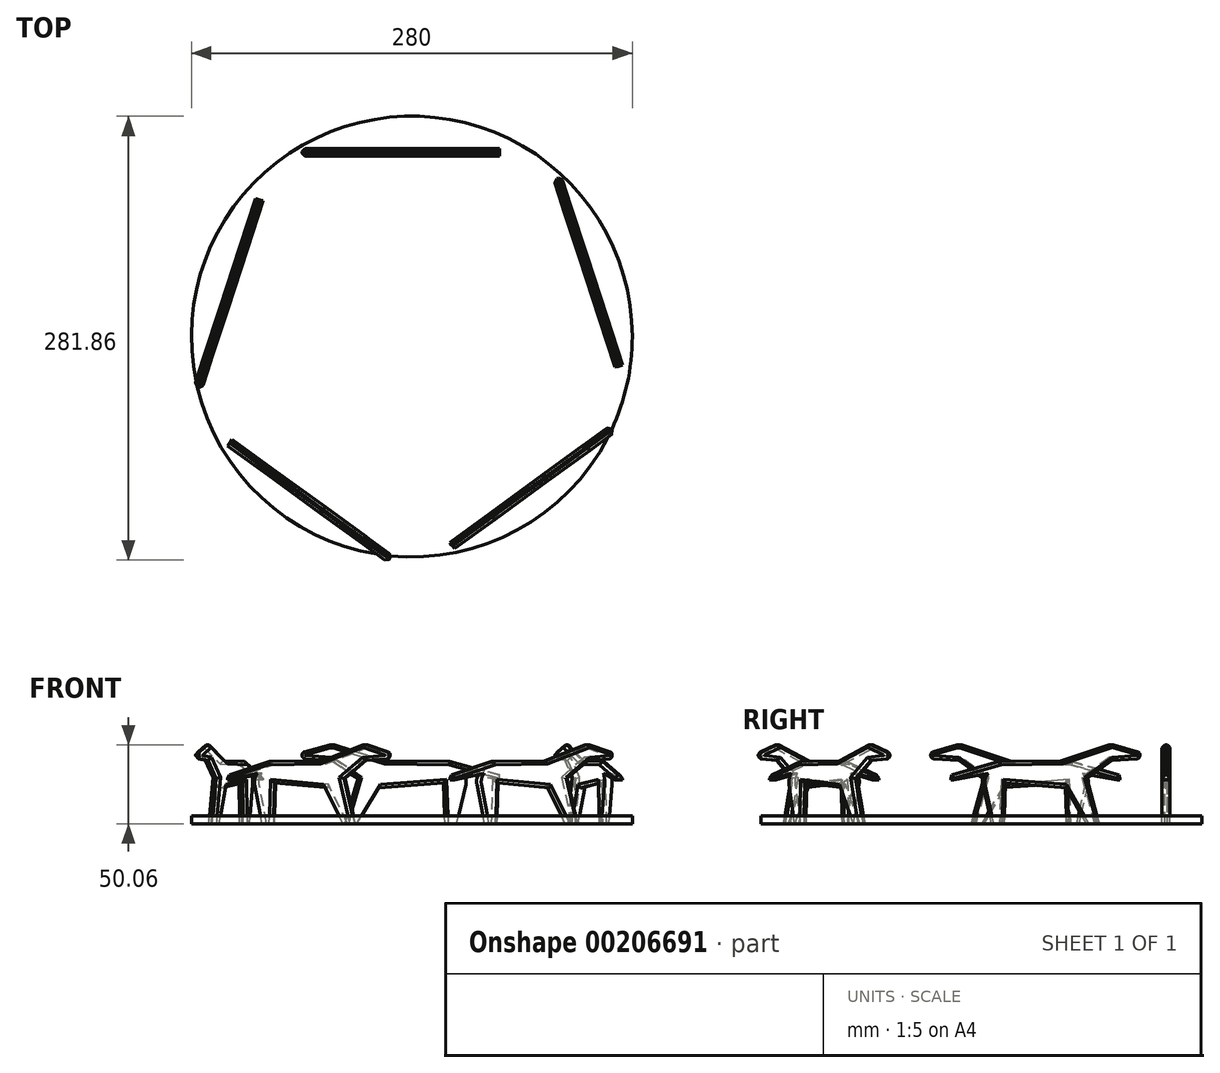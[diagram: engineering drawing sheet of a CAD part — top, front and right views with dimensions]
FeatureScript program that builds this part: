
annotation { "Feature Type Name" : "Feature", "Feature Type Description" : "" }
export const myFeature = defineFeature(function(context is Context, id is Id, definition is map)
    precondition{}
    {
        {
            var Q0;
            Q0=qCreatedBy(makeId("Front.planeOp"),FACE);
            var sketch = newSketch(context, id + "F0", { "sketchPlane" : qUnion([Q0])});
            skLineSegment(sketch, "E0", {"start": v(0, 30.49) * mm, "end": v(0, -33.76) * mm, "construction": true});
            skLineSegment(sketch, "E1", {"start": v(-37.33, 0) * mm, "end": v(42.96, 0) * mm, "construction": true});
            skArc(sketch, "E2", {"start": v(-21.11, 22.86) * mm, "mid": v(-24.39, 33.27) * mm, "end": v(-34.27, 28.64) * mm});
            skArc(sketch, "E3.MirrorC", {"start": v(20.07, 26.07) * mm, "mid": v(27.86, 33.86) * mm, "end": v(34.36, 24.97) * mm});
            skLineSegment(sketch, "E4", {"start": v(-42.5, 0) * mm, "end": v(-35.04, 0) * mm});
            skLineSegment(sketch, "E5", {"start": v(-35.04, 0) * mm, "end": v(-21.11, 22.86) * mm});
            skLineSegment(sketch, "E6", {"start": v(-42.5, 0) * mm, "end": v(-34.27, 28.64) * mm});
            skLineSegment(sketch, "E7", {"start": v(21.03, 0) * mm, "end": v(28.49, 0) * mm});
            skLineSegment(sketch, "E8", {"start": v(28.49, 0) * mm, "end": v(34.36, 24.97) * mm});
            skLineSegment(sketch, "E9", {"start": v(21.03, 0) * mm, "end": v(20.06, 26.37) * mm});
            skLineSegment(sketch, "E10", {"start": v(-21.11, 22.86) * mm, "end": v(20.07, 26.07) * mm});
            skArc(sketch, "E11", {"start": v(-52.04, 50.06) * mm, "mid": v(-50.83, 40.22) * mm, "end": v(-49.22, 50) * mm});
            skCircle(sketch, "E12", {"center": v(-67.49, 43.52) * mm, "radius": 2.27 * mm});
            skLineSegment(sketch, "E13", {"start": v(-68.08, 45.71) * mm, "end": v(-52.04, 50.06) * mm});
            skLineSegment(sketch, "E14", {"start": v(-67.63, 41.25) * mm, "end": v(-51.04, 40.22) * mm});
            skLineSegment(sketch, "E15", {"start": v(-51.04, 40.22) * mm, "end": v(-34.27, 28.64) * mm});
            skLineSegment(sketch, "E16", {"start": v(-49.22, 50) * mm, "end": v(-17.15, 39.88) * mm});
            skLineSegment(sketch, "E17", {"start": v(-17.15, 39.88) * mm, "end": v(24.08, 39.47) * mm});
            skLineSegment(sketch, "E18", {"start": v(24.08, 39.47) * mm, "end": v(55.59, 30.9) * mm});
            skLineSegment(sketch, "E19", {"start": v(55.59, 30.9) * mm, "end": v(55.59, 27.7) * mm});
            skLineSegment(sketch, "E20", {"start": v(55.59, 27.7) * mm, "end": v(32.22, 31.96) * mm});
            skLineSegment(sketch, "E21", {"start": v(-52.04, 50.06) * mm, "end": v(-49.22, 50) * mm});
            skSolve(sketch);
        }
        {
            var Q0;
            Q0 = qSketchRegion(id + "F0", true);
            extrude(context, id + "F1", {"entities" : qUnion([Q0]), "endBound" : BoundingType.SYMMETRIC, "depth" : 5 * mm});
        }
        {
            var Q0;
            Q0=makeQuery(id+"F1.opExtrude","CAP_EDGE",EDGE,{"disambiguationData":[OSD([sQuery(id+"F0.wireOp",EDGE,"E13")])],"isStart":false});
            var Q1;
            Q1=makeQuery(id+"F1.opExtrude","CAP_EDGE",EDGE,{"disambiguationData":[OSD([sQuery(id+"F0.wireOp",EDGE,"E21")])],"isStart":false});
            var Q2;
            Q2=makeQuery(id+"F1.opExtrude","CAP_EDGE",EDGE,{"disambiguationData":[OSD([sQuery(id+"F0.wireOp",EDGE,"E15")])],"isStart":false});
            var Q3;
            Q3=makeQuery(id+"F1.opExtrude","CAP_EDGE",EDGE,{"disambiguationData":[OSD([sQuery(id+"F0.wireOp",EDGE,"E6")])],"isStart":false});
            var Q4;
            Q4=makeQuery(id+"F1.opExtrude","CAP_EDGE",EDGE,{"disambiguationData":[OSD([sQuery(id+"F0.wireOp",EDGE,"E10")])],"isStart":false});
            var Q5;
            Q5=makeQuery(id+"F1.opExtrude","CAP_EDGE",EDGE,{"disambiguationData":[OSD([sQuery(id+"F0.wireOp",EDGE,"E9")])],"isStart":false});
            var Q6;
            Q6=makeQuery(id+"F1.opExtrude","CAP_EDGE",EDGE,{"disambiguationData":[OSD([sQuery(id+"F0.wireOp",EDGE,"E16")])],"isStart":false});
            var Q7;
            Q7=makeQuery(id+"F1.opExtrude","CAP_EDGE",EDGE,{"disambiguationData":[OSD([sQuery(id+"F0.wireOp",EDGE,"E17")])],"isStart":false});
            var Q8;
            Q8=makeQuery(id+"F1.opExtrude","CAP_EDGE",EDGE,{"disambiguationData":[OSD([sQuery(id+"F0.wireOp",EDGE,"E18")])],"isStart":false});
            var Q9;
            Q9=makeQuery(id+"F1.opExtrude","CAP_EDGE",EDGE,{"disambiguationData":[OSD([sQuery(id+"F0.wireOp",EDGE,"E18")])],"isStart":true});
            var Q10;
            Q10=makeQuery(id+"F1.opExtrude","CAP_EDGE",EDGE,{"disambiguationData":[OSD([sQuery(id+"F0.wireOp",EDGE,"E17")])],"isStart":true});
            var Q11;
            Q11=makeQuery(id+"F1.opExtrude","CAP_EDGE",EDGE,{"disambiguationData":[OSD([sQuery(id+"F0.wireOp",EDGE,"E16")])],"isStart":true});
            var Q12;
            Q12=makeQuery(id+"F1.opExtrude","CAP_EDGE",EDGE,{"disambiguationData":[OSD([sQuery(id+"F0.wireOp",EDGE,"E13")])],"isStart":true});
            var Q13;
            Q13=makeQuery(id+"F1.opExtrude","CAP_EDGE",EDGE,{"disambiguationData":[OSD([sQuery(id+"F0.wireOp",EDGE,"E15")])],"isStart":true});
            var Q14;
            Q14=makeQuery(id+"F1.opExtrude","CAP_EDGE",EDGE,{"disambiguationData":[OSD([sQuery(id+"F0.wireOp",EDGE,"E6")])],"isStart":true});
            var Q15;
            Q15=makeQuery(id+"F1.opExtrude","CAP_EDGE",EDGE,{"disambiguationData":[OSD([sQuery(id+"F0.wireOp",EDGE,"E10")])],"isStart":true});
            var Q16;
            Q16=makeQuery(id+"F1.opExtrude","CAP_EDGE",EDGE,{"disambiguationData":[OSD([sQuery(id+"F0.wireOp",EDGE,"E9")])],"isStart":true});
            chamfer(context, id + "F2", {"entities" : qUnion([Q0, Q1, Q2, Q3, Q4, Q5, Q6, Q7, Q8, Q9, Q10, Q11, Q12, Q13, Q14, Q15, Q16]), "width" : 2 * mm, "tangentPropagation" : true});
        }
        {
            var Q0;
            Q0=qCreatedBy(makeId("Right.planeOp"),FACE);
            var sketch = newSketch(context, id + "F3", { "sketchPlane" : qUnion([Q0])});
            skLineSegment(sketch, "E22", {"start": v(-120, 99.8) * mm, "end": v(-120, -76.05) * mm, "construction": true});
            skSolve(sketch);
        }
        {
            var Q0;
            Q0=makeQuery(id+"F1.opExtrude","SWEPT_BODY",BODY,{"disambiguationData":[OSD([sQuery(id+"F0.wireOp",EDGE,"E3.MirrorC"),sQuery(id+"F0.wireOp",EDGE,"E4"),sQuery(id+"F0.wireOp",EDGE,"E5"),sQuery(id+"F0.wireOp",EDGE,"E6"),sQuery(id+"F0.wireOp",EDGE,"E7"),sQuery(id+"F0.wireOp",EDGE,"E8"),sQuery(id+"F0.wireOp",EDGE,"E9"),sQuery(id+"F0.wireOp",EDGE,"E10"),sQuery(id+"F0.wireOp",EDGE,"E12"),sQuery(id+"F0.wireOp",EDGE,"E13"),sQuery(id+"F0.wireOp",EDGE,"E14"),sQuery(id+"F0.wireOp",EDGE,"E15"),sQuery(id+"F0.wireOp",EDGE,"E16"),sQuery(id+"F0.wireOp",EDGE,"E17"),sQuery(id+"F0.wireOp",EDGE,"E18"),sQuery(id+"F0.wireOp",EDGE,"E19"),sQuery(id+"F0.wireOp",EDGE,"E20"),sQuery(id+"F0.wireOp",EDGE,"E21")])]});
            var Q1;
            Q1=sQuery(id+"F3.wireOp",EDGE,"E22");
            circularPattern(context, id + "F4", {"entities" : qUnion([Q0]), "axis" : qUnion([Q1]), "angle" : 360 * degree, "instanceCount" : 5, "equalSpace" : true});
        }
        {
            var Q0;
            Q0=qCreatedBy(makeId("Top.planeOp"),FACE);
            var sketch = newSketch(context, id + "F5", { "sketchPlane" : qUnion([Q0])});
            skCircle(sketch, "E23", {"center": v(0, -117.07) * mm, "radius": 140 * mm});
            skSolve(sketch);
        }
        {
            var Q0;
            Q0 = qSketchRegion(id + "F5", true);
            extrude(context, id + "F6", {"entities" : qUnion([Q0]), "depth" : 5 * mm});
        }
    });
